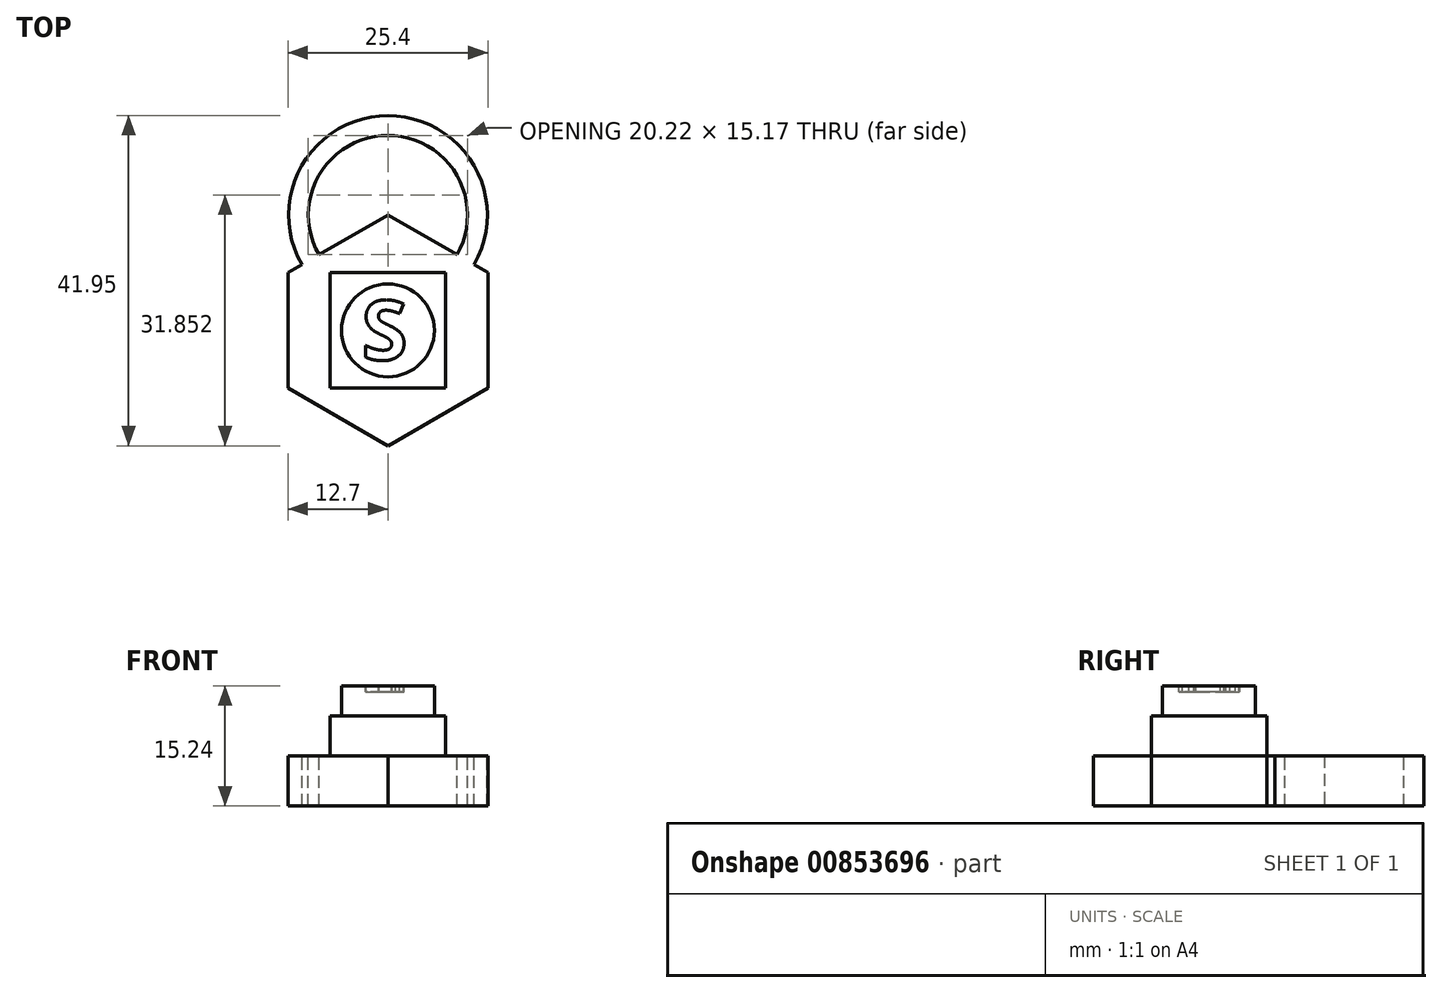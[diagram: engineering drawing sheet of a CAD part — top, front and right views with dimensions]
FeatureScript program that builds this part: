
annotation { "Feature Type Name" : "Feature", "Feature Type Description" : "" }
export const myFeature = defineFeature(function(context is Context, id is Id, definition is map)
    precondition{}
    {
        {
            var Q0;
            Q0=qCreatedBy(makeId("Top.planeOp"),FACE);
            var sketch = newSketch(context, id + "F0", { "sketchPlane" : qUnion([Q0])});
            skCircle(sketch, "E0.cCircle", {"center": v(0, 0) * mm, "radius": 12.7 * mm, "construction": true});
            skLineSegment(sketch, "E0.0", {"start": v(12.7, 7.33) * mm, "end": v(12.7, -7.33) * mm});
            skLineSegment(sketch, "E0.1", {"start": v(12.7, -7.33) * mm, "end": v(0, -14.66) * mm});
            skLineSegment(sketch, "E0.2", {"start": v(0, -14.66) * mm, "end": v(-12.7, -7.33) * mm});
            skLineSegment(sketch, "E0.3", {"start": v(-12.7, -7.33) * mm, "end": v(-12.7, 7.33) * mm});
            skLineSegment(sketch, "E0.4", {"start": v(-12.7, 7.33) * mm, "end": v(0, 14.66) * mm});
            skLineSegment(sketch, "E0.5", {"start": v(0, 14.66) * mm, "end": v(12.7, 7.33) * mm});
            skPoint(sketch, "E0.0.midPoint", {"position": v(12.7, 0) * mm});
            skSolve(sketch);
        }
        {
            var Q0;
            Q0=makeQuery(id+"F0.imprint","IMPRINT",FACE,{"disambiguationData":[TD([[makeQuery(id+"F0.imprint","IMPRINT",EDGE,{"derivedFrom":sQuery(id+"F0.wireOp",EDGE,"E0.0")}),-1.0]])]});
            extrude(context, id + "F1", {"entities" : qUnion([Q0]), "depth" : 6.35 * mm, "offsetDistance" : 25.4 * mm});
        }
        {
            var Q0;
            Q0=makeQuery(id+"F1.opExtrude","CAP_FACE",FACE,{"disambiguationData":[OSD([sQuery(id+"F0.wireOp",EDGE,"E0.0"),sQuery(id+"F0.wireOp",EDGE,"E0.1"),sQuery(id+"F0.wireOp",EDGE,"E0.2"),sQuery(id+"F0.wireOp",EDGE,"E0.3"),sQuery(id+"F0.wireOp",EDGE,"E0.4"),sQuery(id+"F0.wireOp",EDGE,"E0.5")])],"isStart":false});
            var sketch = newSketch(context, id + "F2", { "sketchPlane" : qUnion([Q0])});
            skCircle(sketch, "E1.cCircle", {"center": v(0, 0) * mm, "radius": 7.33 * mm, "construction": true});
            skLineSegment(sketch, "E1.0", {"start": v(-7.33, 7.33) * mm, "end": v(7.33, 7.33) * mm});
            skLineSegment(sketch, "E1.1", {"start": v(7.33, 7.33) * mm, "end": v(7.33, -7.33) * mm});
            skLineSegment(sketch, "E1.2", {"start": v(7.33, -7.33) * mm, "end": v(-7.33, -7.33) * mm});
            skLineSegment(sketch, "E1.3", {"start": v(-7.33, -7.33) * mm, "end": v(-7.33, 7.33) * mm});
            skPoint(sketch, "E1.0.midPoint", {"position": v(0, 7.33) * mm});
            skSolve(sketch);
        }
        {
            var Q0;
            Q0=makeQuery(id+"F2.imprint","IMPRINT",FACE,{"disambiguationData":[TD([[makeQuery(id+"F2.imprint","IMPRINT",EDGE,{"derivedFrom":sQuery(id+"F2.wireOp",EDGE,"E1.0")}),-1.0]])]});
            extrude(context, id + "F3", {"entities" : qUnion([Q0]), "operationType" : NewBodyOperationType.ADD, "depth" : 5.08 * mm, "offsetDistance" : 25.4 * mm});
        }
        {
            var Q0;
            Q0=makeQuery(id+"F3.opExtrude","CAP_FACE",FACE,{"disambiguationData":[OSD([sQuery(id+"F2.wireOp",EDGE,"E1.0"),sQuery(id+"F2.wireOp",EDGE,"E1.1"),sQuery(id+"F2.wireOp",EDGE,"E1.2"),sQuery(id+"F2.wireOp",EDGE,"E1.3")])],"isStart":false});
            var sketch = newSketch(context, id + "F4", { "sketchPlane" : qUnion([Q0])});
            skCircle(sketch, "E2", {"center": v(0, 0) * mm, "radius": 5.9 * mm});
            skSolve(sketch);
        }
        {
            var Q0;
            Q0=makeQuery(id+"F4.imprint","IMPRINT",FACE,{"disambiguationData":[TD([[makeQuery(id+"F4.imprint","IMPRINT",EDGE,{"derivedFrom":sQuery(id+"F4.wireOp",EDGE,"E2")}),1.0]])]});
            extrude(context, id + "F5", {"entities" : qUnion([Q0]), "operationType" : NewBodyOperationType.ADD, "depth" : 3.8 * mm, "offsetDistance" : 25.4 * mm});
        }
        {
            var Q0;
            Q0=makeQuery(id+"F5.opExtrude","CAP_FACE",FACE,{"disambiguationData":[OSD([sQuery(id+"F4.wireOp",EDGE,"E2")])],"isStart":false});
            var sketch = newSketch(context, id + "F6", { "sketchPlane" : qUnion([Q0])});
            skText(sketch, "E3", { "text": "S", "fontName": "OpenSans-Bold.ttf"});
            const initialGuessF6  = {"E3": [-0.00334, -0.00374, 1, 0, 0.00759]};
            skSetInitialGuess(sketch, initialGuessF6);
            skSolve(sketch);
        }
        {
            var Q0;
            Q0 = qSketchRegion(id + "F6", true);
            extrude(context, id + "F7", {"entities" : qUnion([Q0]), "operationType" : NewBodyOperationType.REMOVE, "depth" : -0.76 * mm, "offsetDistance" : 25.4 * mm});
        }
        {
            var Q0;
            Q0=makeQuery(id+"F1.opExtrude","CAP_FACE",FACE,{"disambiguationData":[OSD([sQuery(id+"F0.wireOp",EDGE,"E0.0"),sQuery(id+"F0.wireOp",EDGE,"E0.1"),sQuery(id+"F0.wireOp",EDGE,"E0.2"),sQuery(id+"F0.wireOp",EDGE,"E0.3"),sQuery(id+"F0.wireOp",EDGE,"E0.4"),sQuery(id+"F0.wireOp",EDGE,"E0.5")])],"isStart":false});
            var sketch = newSketch(context, id + "F8", { "sketchPlane" : qUnion([Q0])});
            skCircle(sketch, "E4", {"center": v(0, 14.66) * mm, "radius": 12.62 * mm});
            skCircle(sketch, "E5", {"center": v(0, 14.66) * mm, "radius": 10.11 * mm});
            skSolve(sketch);
        }
        {
            var Q0;
            Q0 = qSketchRegion(id + "F8", true);
            var Q1;
            Q1=makeQuery(id+"F1.opExtrude","CAP_FACE",FACE,{"disambiguationData":[OSD([sQuery(id+"F0.wireOp",EDGE,"E0.0"),sQuery(id+"F0.wireOp",EDGE,"E0.1"),sQuery(id+"F0.wireOp",EDGE,"E0.2"),sQuery(id+"F0.wireOp",EDGE,"E0.3"),sQuery(id+"F0.wireOp",EDGE,"E0.4"),sQuery(id+"F0.wireOp",EDGE,"E0.5")])],"isStart":true});
            extrude(context, id + "F9", {"entities" : qUnion([Q0]), "operationType" : NewBodyOperationType.ADD, "endBound" : BoundingType.UP_TO_SURFACE, "oppositeDirection" : true, "depth" : 6.35 * mm, "endBoundEntityFace" : qUnion([Q1]), "offsetDistance" : 25.4 * mm});
        }
    });
